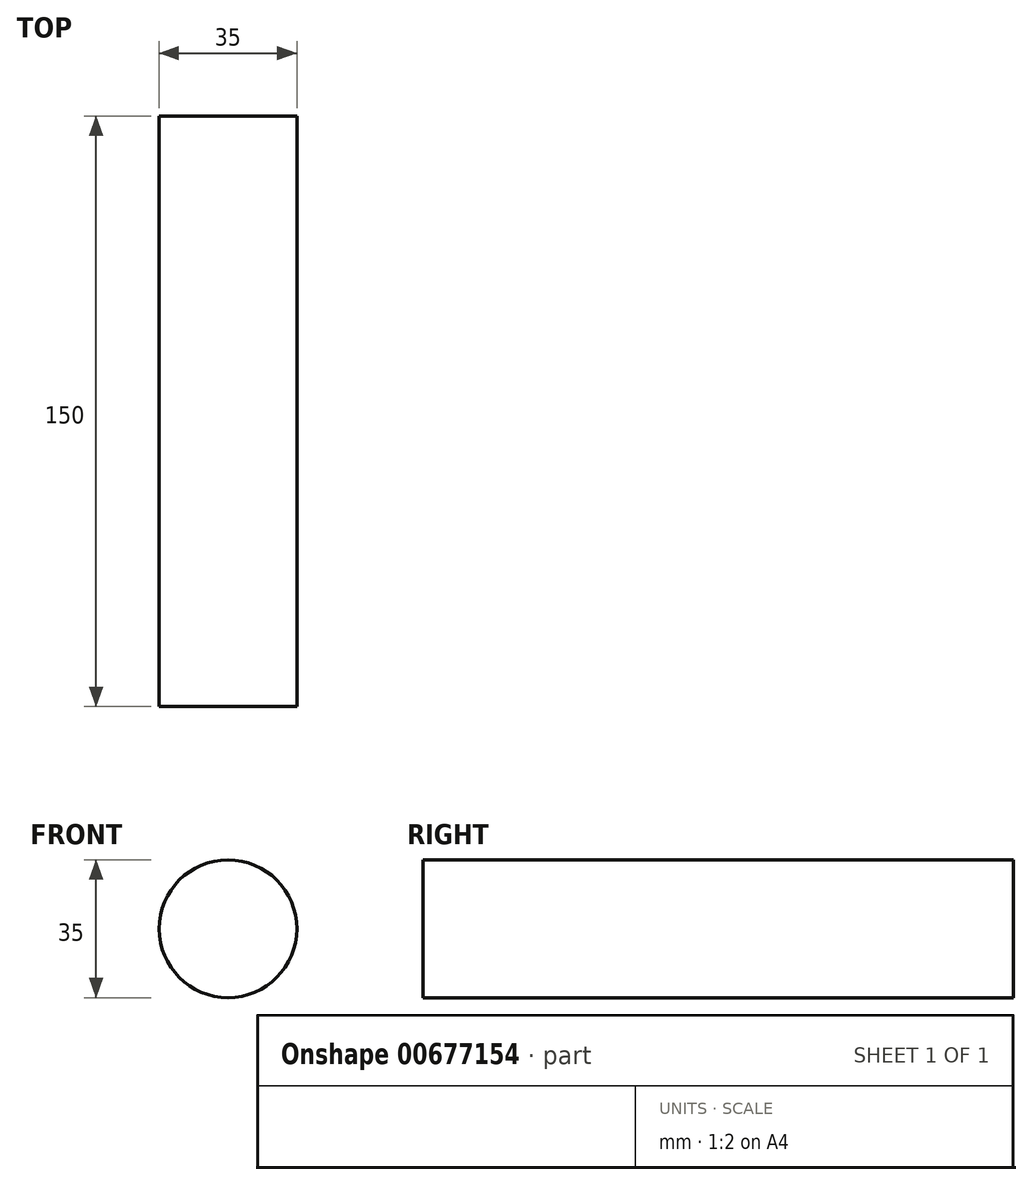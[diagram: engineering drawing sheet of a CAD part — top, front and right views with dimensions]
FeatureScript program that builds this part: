
annotation { "Feature Type Name" : "Feature", "Feature Type Description" : "" }
export const myFeature = defineFeature(function(context is Context, id is Id, definition is map)
    precondition{}
    {
        {
            var Q0;
            Q0=qCreatedBy(makeId("Front.planeOp"),FACE);
            var sketch = newSketch(context, id + "F0", { "sketchPlane" : qUnion([Q0])});
            skCircle(sketch, "E0", {"center": v(0, 0) * mm, "radius": 17.5 * mm});
            skSolve(sketch);
        }
        {
            var Q0;
            Q0=makeQuery(id+"F0.imprint","IMPRINT",FACE,{"disambiguationData":[TD([[makeQuery(id+"F0.imprint","IMPRINT",EDGE,{"derivedFrom":sQuery(id+"F0.wireOp",EDGE,"E0")}),1.0]])]});
            extrude(context, id + "F1", {"entities" : qUnion([Q0]), "depth" : 150 * mm, "offsetDistance" : 25 * mm});
        }
    });
